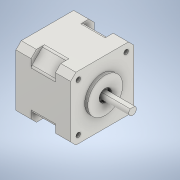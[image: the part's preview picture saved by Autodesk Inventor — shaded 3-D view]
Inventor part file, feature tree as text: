
AUTODESK INVENTOR PART (.ipt)
format: ipt  version: 2021 (Build 250183000, 183)  size: 231,424 bytes
history: native  units: mm
features: extrude x8, sketch x7, chamfer x1, fillet x1
ambient origin geometry x8: Origin, YZ Plane, XZ Plane, XY Plane, X Axis, Y Axis, Z Axis, Center Point
bodies: Volumenkörper1 (feature_tree)
feature tree (17):
  extrude  "Extrusion1"  Depth=41.5mm
  chamfer  "Fase1"  Distance=10.0mm
  extrude  "Extrusion5"  Depth=41.5mm
  extrude  "Extrusion6"  Depth=8.0mm
  fillet  "Rundung1"  Radius=8.0mm
  sketch  "Skizze7"  dims[d22=40.0mm d24=360.0deg d26=16.0mm d27=0.0mm]
  extrude  "Extrusion7"  Depth=16.0mm TaperAngle=0.0deg
  extrude  "Extrusion8"  Depth=41.5mm
  extrude  "Extrusion9"  Depth=10.0mm TaperAngle=0.0deg
  extrude  "Extrusion10"  Depth=8.0mm
  extrude  "Extrusion11"  Depth=2.0mm TaperAngle=0.0deg
  sketch  "Skizze2"  dims[d0=41.5mm d1=41.5mm d2=10.0mm d3=0.0mm]
  sketch  "Skizze5"  dims[d8=3.5mm d9=2.0mm d10=45.0deg d11=41.5mm]
  sketch  "Skizze6"  dims[d12=41.5mm d20=8.0mm d21=8.0mm]
  sketch  "Skizze8"  dims[d28=41.5mm d29=41.5mm]
  sketch  "Skizze9"  dims[d30=40.0mm d32=360.0deg d34=10.0mm d35=0.0mm]
  sketch  "Skizze10"  dims[d36=2.0mm d37=23.0mm d38=2.0mm d39=0.0mm d40=8.0mm d41=2.0mm d42=0.0mm d43=5.0mm d44=0.5mm d45=20.0mm d46=0.0mm d47=2.0mm d48=10.0mm d49=15.0mm d50=4.0mm d51=0.0mm d61=3.0mm d62=3.0mm d67=15.75mm d68=15.75mm d69=3.0mm d70=3.0mm d71=15.75mm d72=15.75mm d73=8.0mm d74=0.0mm]
